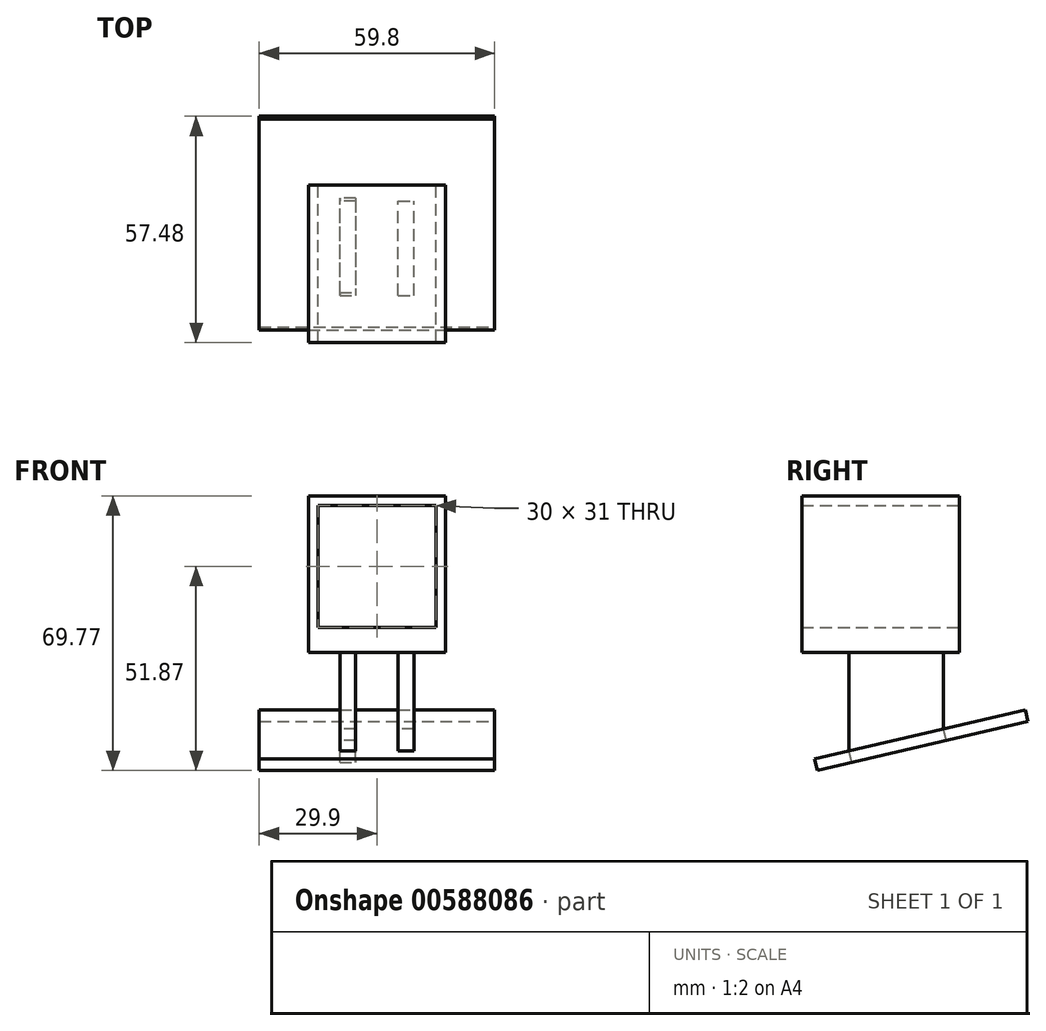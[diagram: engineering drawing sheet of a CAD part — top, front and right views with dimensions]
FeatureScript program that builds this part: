
annotation { "Feature Type Name" : "Feature", "Feature Type Description" : "" }
export const myFeature = defineFeature(function(context is Context, id is Id, definition is map)
    precondition{}
    {
        {
            var Q0;
            Q0=qCreatedBy(makeId("Front.planeOp"),FACE);
            var sketch = newSketch(context, id + "F0", { "sketchPlane" : qUnion([Q0])});
            skLineSegment(sketch, "E0.bottom", {"start": v(0, 0) * mm, "end": v(-30, 0) * mm});
            skLineSegment(sketch, "E0.top", {"start": v(0, 35) * mm, "end": v(-30, 35) * mm});
            skLineSegment(sketch, "E0.left", {"start": v(0, 0) * mm, "end": v(0, 35) * mm});
            skLineSegment(sketch, "E0.right", {"start": v(-30, 0) * mm, "end": v(-30, 35) * mm});
            skLineSegment(sketch, "E1.bottom", {"start": v(2.4, -2.4) * mm, "end": v(-32.4, -2.4) * mm});
            skLineSegment(sketch, "E1.top", {"start": v(2.4, 37.4) * mm, "end": v(-32.4, 37.4) * mm});
            skLineSegment(sketch, "E1.left", {"start": v(2.4, -2.4) * mm, "end": v(2.4, 37.4) * mm});
            skLineSegment(sketch, "E1.right", {"start": v(-32.4, -2.4) * mm, "end": v(-32.4, 37.4) * mm});
            skSolve(sketch);
        }
        {
            var Q0;
            Q0=makeQuery(id+"F0.imprint","IMPRINT",FACE,{"disambiguationData":[TD([[makeQuery(id+"F0.imprint","IMPRINT",EDGE,{"derivedFrom":sQuery(id+"F0.wireOp",EDGE,"E0.bottom")}),1.0]])]});
            extrude(context, id + "F1", {"entities" : qUnion([Q0]), "depth" : 40 * mm, "offsetDistance" : 25 * mm});
        }
        {
            var Q0;
            Q0=makeQuery(id+"F1.opExtrude","SWEPT_FACE",FACE,{"disambiguationData":[OSD([sQuery(id+"F0.wireOp",EDGE,"E1.bottom")])]});
            var sketch = newSketch(context, id + "F2", { "sketchPlane" : qUnion([Q0])});
            skLineSegment(sketch, "E2.bottom", {"start": v(-24.4, 28) * mm, "end": v(-20.4, 28) * mm});
            skLineSegment(sketch, "E2.top", {"start": v(-24.4, 4) * mm, "end": v(-20.4, 4) * mm});
            skLineSegment(sketch, "E2.left", {"start": v(-24.4, 28) * mm, "end": v(-24.4, 4) * mm});
            skLineSegment(sketch, "E2.right", {"start": v(-20.4, 28) * mm, "end": v(-20.4, 4) * mm});
            skLineSegment(sketch, "E3.bottom", {"start": v(-9.6, 28) * mm, "end": v(-5.6, 28) * mm});
            skLineSegment(sketch, "E3.top", {"start": v(-9.6, 4) * mm, "end": v(-5.6, 4) * mm});
            skLineSegment(sketch, "E3.left", {"start": v(-9.6, 28) * mm, "end": v(-9.6, 4) * mm});
            skLineSegment(sketch, "E3.right", {"start": v(-5.6, 28) * mm, "end": v(-5.6, 4) * mm});
            skSolve(sketch);
        }
        {
            var Q0;
            Q0=makeQuery(id+"F2.imprint","IMPRINT",FACE,{"disambiguationData":[TD([[makeQuery(id+"F2.imprint","IMPRINT",EDGE,{"derivedFrom":sQuery(id+"F2.wireOp",EDGE,"E2.bottom")}),-1.0]])]});
            var Q1;
            Q1=makeQuery(id+"F2.imprint","IMPRINT",FACE,{"disambiguationData":[TD([[makeQuery(id+"F2.imprint","IMPRINT",EDGE,{"derivedFrom":sQuery(id+"F2.wireOp",EDGE,"E3.bottom")}),-1.0]])]});
            extrude(context, id + "F3", {"entities" : qUnion([Q0, Q1]), "operationType" : NewBodyOperationType.ADD, "depth" : 25 * mm, "offsetDistance" : 25 * mm});
        }
        {
            var Q0;
            Q0=makeQuery(id+"F3.opExtrude","SWEPT_FACE",FACE,{"disambiguationData":[OSD([sQuery(id+"F2.wireOp",EDGE,"E2.left")])]});
            var sketch = newSketch(context, id + "F4", { "sketchPlane" : qUnion([Q0])});
            skLineSegment(sketch, "E4", {"start": v(28, -27.4) * mm, "end": v(4, -21.8) * mm});
            skSolve(sketch);
        }
        {
            var Q0;
            {var subQ0=sQuery(id+"F4.wireOp",EDGE,"E4");Q0=makeQuery(id+"F4.imprint","IMPRINT",FACE,{"disambiguationData":[TD([[makeQuery(id+"F4.imprint","IMPRINT",EDGE,{"derivedFrom":subQ0}),1.0]])]});}
            extrude(context, id + "F5", {"entities" : qUnion([Q0]), "operationType" : NewBodyOperationType.REMOVE, "oppositeDirection" : true, "depth" : 25 * mm, "offsetDistance" : 25 * mm});
        }
        {
            var Q0;
            Q0=makeQuery(id+"F1.opExtrude","SWEPT_FACE",FACE,{"disambiguationData":[OSD([sQuery(id+"F0.wireOp",EDGE,"E0.bottom")])]});
            extrude(context, id + "F6", {"entities" : qUnion([Q0]), "operationType" : NewBodyOperationType.ADD, "depth" : 4 * mm, "offsetDistance" : 25 * mm});
        }
        {
            var Q0;
            Q0=makeQuery(id+"F5.boolean.opBoolean","COPY",FACE,{"disambiguationData":[TD([makeQuery(id+"F3.opExtrude","SWEPT_FACE",FACE,{"disambiguationData":[OSD([sQuery(id+"F2.wireOp",EDGE,"E2.bottom")])]})])],"derivedFrom":makeQuery(id+"F5.opExtrude","SWEPT_FACE",FACE,{"disambiguationData":[OSD([sQuery(id+"F4.wireOp",EDGE,"E4")])]})});
            var sketch = newSketch(context, id + "F7", { "sketchPlane" : qUnion([Q0])});
            skLineSegment(sketch, "E5.bottom", {"start": v(-44.9, 42.5) * mm, "end": v(14.9, 42.5) * mm});
            skLineSegment(sketch, "E5.top", {"start": v(-44.9, -12.5) * mm, "end": v(14.9, -12.5) * mm});
            skLineSegment(sketch, "E5.left", {"start": v(-44.9, 42.5) * mm, "end": v(-44.9, -12.5) * mm});
            skLineSegment(sketch, "E5.right", {"start": v(14.9, 42.5) * mm, "end": v(14.9, -12.5) * mm});
            skSolve(sketch);
        }
        {
            var Q0;
            Q0=makeQuery(id+"F7.imprint","IMPRINT",FACE,{"disambiguationData":[TD([[makeQuery(id+"F7.imprint","IMPRINT",EDGE,{"derivedFrom":sQuery(id+"F7.wireOp",EDGE,"E5.bottom")}),-1.0]])]});
            var Q1;
            {var subQ0=sQuery(id+"F4.wireOp",EDGE,"E4");Q1=makeQuery(id+"F7.imprint","IMPRINT",FACE,{"disambiguationData":[TD([[makeQuery(id+"F7.imprint","IMPRINT",EDGE,{"derivedFrom":makeQuery(id+"F5.boolean.opBoolean","COPY",EDGE,{"derivedFrom":makeQuery(id+"F5.opExtrude","CAP_EDGE",EDGE,{"disambiguationData":[OSD([subQ0])],"isStart":true})})}),1.0]])]});}
            extrude(context, id + "F8", {"entities" : qUnion([Q0, Q1]), "depth" : 3 * mm, "offsetDistance" : 25 * mm});
        }
    });
